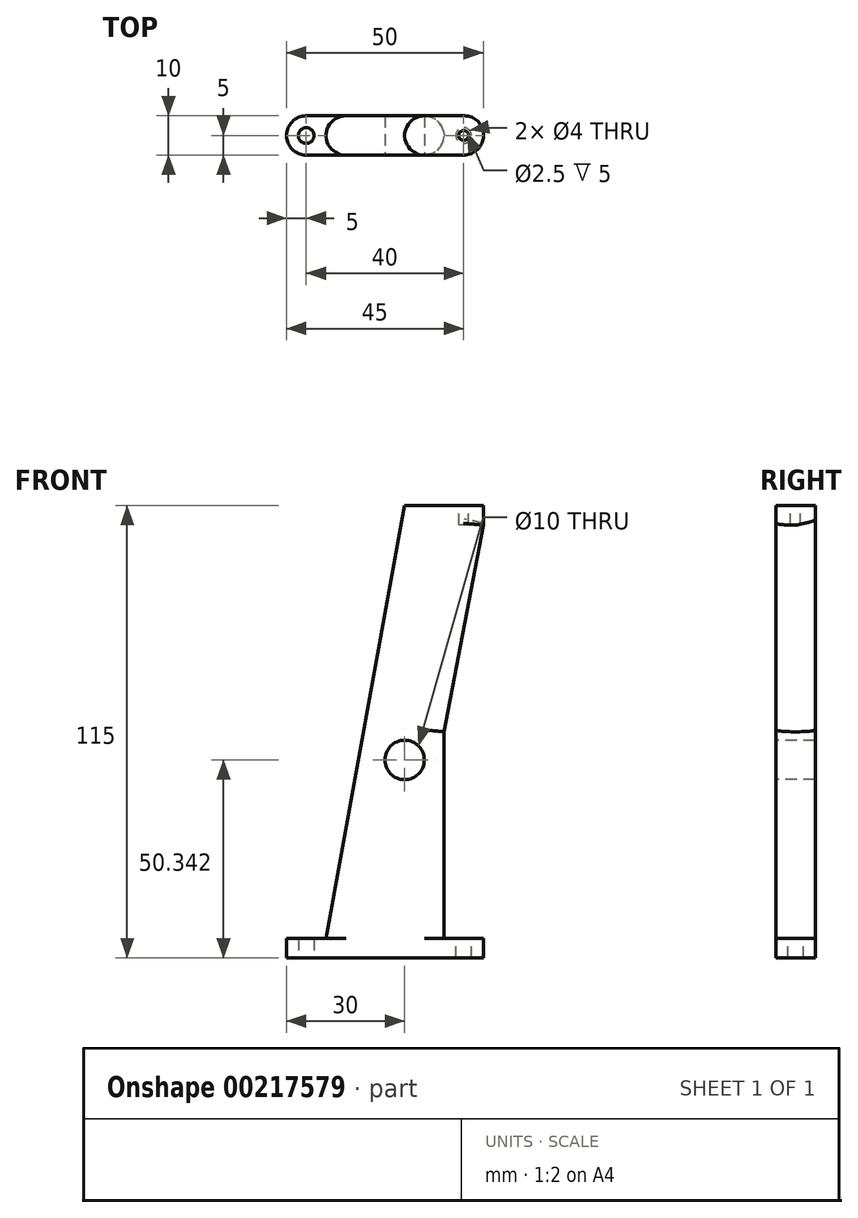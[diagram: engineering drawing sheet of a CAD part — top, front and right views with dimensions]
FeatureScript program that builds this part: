
annotation { "Feature Type Name" : "Feature", "Feature Type Description" : "" }
export const myFeature = defineFeature(function(context is Context, id is Id, definition is map)
    precondition{}
    {
        {
            var Q0;
            Q0=qCreatedBy(makeId("Front.planeOp"),FACE);
            var sketch = newSketch(context, id + "F0", { "sketchPlane" : qUnion([Q0])});
            skLineSegment(sketch, "E0.bottom", {"start": v(0, 0) * mm, "end": v(10, 0) * mm});
            skLineSegment(sketch, "E0.top", {"start": v(0, 115) * mm, "end": v(10, 115) * mm});
            skLineSegment(sketch, "E0.left", {"start": v(0, 0) * mm, "end": v(0, 115) * mm});
            skLineSegment(sketch, "E0.right", {"start": v(10, 5) * mm, "end": v(10, 110) * mm});
            skLineSegment(sketch, "E1.bottom", {"start": v(10, 115) * mm, "end": v(20, 115) * mm});
            skLineSegment(sketch, "E1.top", {"start": v(10, 110) * mm, "end": v(20, 110) * mm});
            skLineSegment(sketch, "E1.right", {"start": v(20, 115) * mm, "end": v(20, 110) * mm});
            skLineSegment(sketch, "E2.bottom", {"start": v(10, 0) * mm, "end": v(20, 0) * mm});
            skLineSegment(sketch, "E2.top", {"start": v(10, 5) * mm, "end": v(20, 5) * mm});
            skLineSegment(sketch, "E2.right", {"start": v(20, 0) * mm, "end": v(20, 5) * mm});
            skSolve(sketch);
        }
        {
            var Q0;
            Q0=makeQuery(id+"F0.imprint","IMPRINT",FACE,{"disambiguationData":[TD([[makeQuery(id+"F0.imprint","IMPRINT",EDGE,{"derivedFrom":sQuery(id+"F0.wireOp",EDGE,"E0.bottom")}),1.0]])]});
            extrude(context, id + "F1", {"entities" : qUnion([Q0]), "depth" : 10 * mm});
        }
        {
            var Q0;
            Q0=makeQuery(id+"F1.opExtrude","SWEPT_FACE",FACE,{"disambiguationData":[OSD([sQuery(id+"F0.wireOp",EDGE,"E0.top"),sQuery(id+"F0.wireOp",EDGE,"E1.bottom")])]});
            var sketch = newSketch(context, id + "F2", { "sketchPlane" : qUnion([Q0])});
            skLineSegment(sketch, "E3.bottom", {"start": v(20, -10) * mm, "end": v(15, -10) * mm, "construction": true});
            skLineSegment(sketch, "E3.top", {"start": v(20, -5) * mm, "end": v(15, -5) * mm, "construction": true});
            skLineSegment(sketch, "E3.left", {"start": v(20, -10) * mm, "end": v(20, -5) * mm, "construction": true});
            skLineSegment(sketch, "E3.right", {"start": v(15, -10) * mm, "end": v(15, -5) * mm, "construction": true});
            skCircle(sketch, "E4", {"center": v(15, -5) * mm, "radius": 2 * mm});
            skLineSegment(sketch, "E5.bottom", {"start": v(15, -10) * mm, "end": v(5, -10) * mm});
            skLineSegment(sketch, "E5.top", {"start": v(15.2, 0) * mm, "end": v(5, 0) * mm});
            skLineSegment(sketch, "E5.left", {"start": v(20, -5) * mm, "end": v(20, -4.8) * mm});
            skLineSegment(sketch, "E5.right", {"start": v(0, -5) * mm, "end": v(0, -5) * mm});
            skPoint(sketch, "E6.visualSharp", {"position": v(0, -10) * mm});
            skArc(sketch, "E6.filletArc", {"start": v(0, -5) * mm, "mid": v(1.46, -8.54) * mm, "end": v(5, -10) * mm});
            skPoint(sketch, "E7.visualSharp", {"position": v(0, 0) * mm});
            skArc(sketch, "E7.filletArc", {"start": v(5, 0) * mm, "mid": v(1.46, -1.46) * mm, "end": v(0, -5) * mm});
            skPoint(sketch, "E8.visualSharp", {"position": v(20, -10) * mm});
            skArc(sketch, "E8.filletArc", {"start": v(15, -10) * mm, "mid": v(18.54, -8.54) * mm, "end": v(20, -5) * mm});
            skPoint(sketch, "E9.visualSharp", {"position": v(20, 0) * mm});
            skArc(sketch, "E9.filletArc", {"start": v(20, -4.8) * mm, "mid": v(18.6, -1.4) * mm, "end": v(15.2, 0) * mm});
            skSolve(sketch);
        }
        {
            var Q0;
            {var subQ0=sQuery(id+"F2.wireOp",EDGE,"E6.filletArc");Q0=makeQuery(id+"F2.imprint","IMPRINT",FACE,{"disambiguationData":[TD([[makeQuery(id+"F2.imprint","IMPRINT",EDGE,{"derivedFrom":subQ0}),-1.0]])]});}
            var Q1;
            {var subQ0=sQuery(id+"F2.wireOp",EDGE,"E7.filletArc");Q1=makeQuery(id+"F2.imprint","IMPRINT",FACE,{"disambiguationData":[TD([[makeQuery(id+"F2.imprint","IMPRINT",EDGE,{"derivedFrom":subQ0}),-1.0]])]});}
            var Q2;
            {var subQ0=sQuery(id+"F2.wireOp",EDGE,"E9.filletArc");Q2=makeQuery(id+"F2.imprint","IMPRINT",FACE,{"disambiguationData":[TD([[makeQuery(id+"F2.imprint","IMPRINT",EDGE,{"derivedFrom":subQ0}),-1.0]])]});}
            var Q3;
            {var subQ0=sQuery(id+"F2.wireOp",EDGE,"E8.filletArc");Q3=makeQuery(id+"F2.imprint","IMPRINT",FACE,{"disambiguationData":[TD([[makeQuery(id+"F2.imprint","IMPRINT",EDGE,{"derivedFrom":subQ0}),-1.0]])]});}
            var Q4;
            Q4=makeQuery(id+"F2.imprint","IMPRINT",FACE,{"disambiguationData":[TD([[makeQuery(id+"F2.imprint","IMPRINT",EDGE,{"derivedFrom":sQuery(id+"F2.wireOp",EDGE,"E4")}),1.0]])]});
            extrude(context, id + "F3", {"entities" : qUnion([Q0, Q1, Q2, Q3, Q4]), "operationType" : NewBodyOperationType.REMOVE, "endBound" : BoundingType.THROUGH_ALL, "oppositeDirection" : true, "depth" : 25 * mm});
        }
        {
            var Q0;
            Q0=makeQuery(id+"F1.opExtrude","SWEPT_FACE",FACE,{"disambiguationData":[OSD([sQuery(id+"F0.wireOp",EDGE,"E0.top"),sQuery(id+"F0.wireOp",EDGE,"E1.bottom")])]});
            var sketch = newSketch(context, id + "F4", { "sketchPlane" : qUnion([Q0])});
            skCircle(sketch, "E10", {"center": v(15, -5) * mm, "radius": 3 * mm});
            skCircle(sketch, "E11", {"center": v(15, -5) * mm, "radius": 1.25 * mm});
            skSolve(sketch);
        }
        {
            var Q0;
            Q0=makeQuery(id+"F4.imprint","IMPRINT",FACE,{"disambiguationData":[TD([[makeQuery(id+"F4.imprint","IMPRINT",EDGE,{"derivedFrom":sQuery(id+"F4.wireOp",EDGE,"E11")}),-1.0]])]});
            extrude(context, id + "F5", {"entities" : qUnion([Q0]), "operationType" : NewBodyOperationType.ADD, "oppositeDirection" : true, "depth" : 5 * mm});
        }
        {
            var Q0;
            Q0=makeQuery(id+"F1.opExtrude","SWEPT_FACE",FACE,{"disambiguationData":[OSD([sQuery(id+"F0.wireOp",EDGE,"E0.bottom"),sQuery(id+"F0.wireOp",EDGE,"E2.bottom")])]});
            var sketch = newSketch(context, id + "F6", { "sketchPlane" : qUnion([Q0])});
            skLineSegment(sketch, "E12.bottom", {"start": v(5, 0) * mm, "end": v(-25, 0) * mm});
            skLineSegment(sketch, "E12.top", {"start": v(5, 10) * mm, "end": v(-25, 10) * mm});
            skLineSegment(sketch, "E12.left", {"start": v(5, 0) * mm, "end": v(5, 10) * mm});
            skLineSegment(sketch, "E12.right", {"start": v(-30, 5) * mm, "end": v(-30, 5) * mm});
            skPoint(sketch, "E13.visualSharp", {"position": v(-30, 0) * mm});
            skArc(sketch, "E13.filletArc", {"start": v(-30, 5) * mm, "mid": v(-28.54, 1.46) * mm, "end": v(-25, 0) * mm});
            skPoint(sketch, "E14.visualSharp", {"position": v(-30, 10) * mm});
            skArc(sketch, "E14.filletArc", {"start": v(-25, 10) * mm, "mid": v(-28.54, 8.54) * mm, "end": v(-30, 5) * mm});
            skCircle(sketch, "E15", {"center": v(-25, 5) * mm, "radius": 2 * mm});
            skSolve(sketch);
        }
        {
            var Q0;
            Q0=makeQuery(id+"F6.imprint","IMPRINT",FACE,{"disambiguationData":[TD([[makeQuery(id+"F6.imprint","IMPRINT",EDGE,{"derivedFrom":sQuery(id+"F6.wireOp",EDGE,"E12.bottom")}),-1.0]])]});
            extrude(context, id + "F7", {"entities" : qUnion([Q0]), "operationType" : NewBodyOperationType.ADD, "oppositeDirection" : true, "depth" : 5 * mm});
        }
        {
            var Q0;
            Q0=makeQuery(id+"F7.boolean.opBoolean","MERGE",FACE,{"derivedFrom":[makeQuery(id+"F1.opExtrude","CAP_FACE",FACE,{"disambiguationData":[OSD([sQuery(id+"F0.wireOp",EDGE,"E0.bottom"),sQuery(id+"F0.wireOp",EDGE,"E0.top"),sQuery(id+"F0.wireOp",EDGE,"E0.left"),sQuery(id+"F0.wireOp",EDGE,"E0.right"),sQuery(id+"F0.wireOp",EDGE,"E1.bottom"),sQuery(id+"F0.wireOp",EDGE,"E1.top"),sQuery(id+"F0.wireOp",EDGE,"E1.right"),sQuery(id+"F0.wireOp",EDGE,"E2.bottom"),sQuery(id+"F0.wireOp",EDGE,"E2.top"),sQuery(id+"F0.wireOp",EDGE,"E2.right")])],"isStart":false}),makeQuery(id+"F7.opExtrude","SWEPT_FACE",FACE,{"disambiguationData":[OSD([sQuery(id+"F6.wireOp",EDGE,"E12.top")])]})]});
            var sketch = newSketch(context, id + "F8", { "sketchPlane" : qUnion([Q0])});
            skLineSegment(sketch, "E16", {"start": v(-25, 5) * mm, "end": v(-20, 5) * mm, "construction": true});
            skLineSegment(sketch, "E17", {"start": v(-20, 5) * mm, "end": v(0, 115) * mm});
            skLineSegment(sketch, "E18", {"start": v(0, 115) * mm, "end": v(5, 115) * mm});
            skLineSegment(sketch, "E19", {"start": v(5, 115) * mm, "end": v(5, 5) * mm});
            skLineSegment(sketch, "E20", {"start": v(5, 5) * mm, "end": v(-20, 5) * mm});
            skSolve(sketch);
        }
        {
            var Q0;
            Q0=makeQuery(id+"F8.imprint","IMPRINT",FACE,{"disambiguationData":[TD([[makeQuery(id+"F8.imprint","IMPRINT",EDGE,{"derivedFrom":sQuery(id+"F8.wireOp",EDGE,"E17")}),-1.0]])]});
            extrude(context, id + "F9", {"entities" : qUnion([Q0]), "operationType" : NewBodyOperationType.ADD, "oppositeDirection" : true, "depth" : 10 * mm});
        }
        {
            var Q0;
            Q0=makeQuery(id+"F9.opExtrude","CAP_EDGE",EDGE,{"disambiguationData":[OSD([sQuery(id+"F8.wireOp",EDGE,"E17")])],"isStart":false});
            var Q1;
            Q1=makeQuery(id+"F9.opExtrude","CAP_EDGE",EDGE,{"disambiguationData":[OSD([sQuery(id+"F8.wireOp",EDGE,"E17")])],"isStart":true});
            fillet(context, id + "F10", {"entities" : qUnion([Q0, Q1]), "radius" : 5 * mm, "tangentPropagation" : true, "allowEdgeOverflow" : false});
        }
        {
            var Q0;
            Q0=makeQuery(id+"F9.boolean.opBoolean","MERGE",FACE,{"derivedFrom":[makeQuery(id+"F7.boolean.opBoolean","MERGE",FACE,{"derivedFrom":[makeQuery(id+"F1.opExtrude","CAP_FACE",FACE,{"disambiguationData":[OSD([sQuery(id+"F0.wireOp",EDGE,"E0.bottom"),sQuery(id+"F0.wireOp",EDGE,"E0.top"),sQuery(id+"F0.wireOp",EDGE,"E0.left"),sQuery(id+"F0.wireOp",EDGE,"E0.right"),sQuery(id+"F0.wireOp",EDGE,"E1.bottom"),sQuery(id+"F0.wireOp",EDGE,"E1.top"),sQuery(id+"F0.wireOp",EDGE,"E1.right"),sQuery(id+"F0.wireOp",EDGE,"E2.bottom"),sQuery(id+"F0.wireOp",EDGE,"E2.top"),sQuery(id+"F0.wireOp",EDGE,"E2.right")])],"isStart":false}),makeQuery(id+"F7.opExtrude","SWEPT_FACE",FACE,{"disambiguationData":[OSD([sQuery(id+"F6.wireOp",EDGE,"E12.top")])]})]}),makeQuery(id+"F9.opExtrude","CAP_FACE",FACE,{"disambiguationData":[OSD([sQuery(id+"F8.wireOp",EDGE,"E17"),sQuery(id+"F8.wireOp",EDGE,"E18"),sQuery(id+"F8.wireOp",EDGE,"E19"),sQuery(id+"F8.wireOp",EDGE,"E20")])],"isStart":true})]});
            var sketch = newSketch(context, id + "F11", { "sketchPlane" : qUnion([Q0])});
            skCircle(sketch, "E21", {"center": v(0, 50.34) * mm, "radius": 5 * mm});
            skSolve(sketch);
        }
        {
            var Q0;
            Q0=makeQuery(id+"F11.imprint","IMPRINT",FACE,{"disambiguationData":[TD([[makeQuery(id+"F11.imprint","IMPRINT",EDGE,{"derivedFrom":sQuery(id+"F11.wireOp",EDGE,"E21")}),1.0]])]});
            extrude(context, id + "F12", {"entities" : qUnion([Q0]), "operationType" : NewBodyOperationType.REMOVE, "endBound" : BoundingType.THROUGH_ALL, "oppositeDirection" : true, "depth" : 25 * mm});
        }
        {
            var Q0;
            Q0=makeQuery(id+"F9.boolean.opBoolean","MERGE",FACE,{"derivedFrom":[makeQuery(id+"F7.boolean.opBoolean","MERGE",FACE,{"derivedFrom":[makeQuery(id+"F1.opExtrude","CAP_FACE",FACE,{"disambiguationData":[OSD([sQuery(id+"F0.wireOp",EDGE,"E0.bottom"),sQuery(id+"F0.wireOp",EDGE,"E0.top"),sQuery(id+"F0.wireOp",EDGE,"E0.left"),sQuery(id+"F0.wireOp",EDGE,"E0.right"),sQuery(id+"F0.wireOp",EDGE,"E1.bottom"),sQuery(id+"F0.wireOp",EDGE,"E1.top"),sQuery(id+"F0.wireOp",EDGE,"E1.right"),sQuery(id+"F0.wireOp",EDGE,"E2.bottom"),sQuery(id+"F0.wireOp",EDGE,"E2.top"),sQuery(id+"F0.wireOp",EDGE,"E2.right")])],"isStart":true}),makeQuery(id+"F7.opExtrude","SWEPT_FACE",FACE,{"disambiguationData":[OSD([sQuery(id+"F6.wireOp",EDGE,"E12.bottom")])]})]}),makeQuery(id+"F9.opExtrude","CAP_FACE",FACE,{"disambiguationData":[OSD([sQuery(id+"F8.wireOp",EDGE,"E17"),sQuery(id+"F8.wireOp",EDGE,"E18"),sQuery(id+"F8.wireOp",EDGE,"E19"),sQuery(id+"F8.wireOp",EDGE,"E20")])],"isStart":false})]});
            var sketch = newSketch(context, id + "F13", { "sketchPlane" : qUnion([Q0])});
            skLineSegment(sketch, "E22", {"start": v(-10, 57.5) * mm, "end": v(-10, 110) * mm});
            skLineSegment(sketch, "E23", {"start": v(-10, 110) * mm, "end": v(-20, 110) * mm});
            skLineSegment(sketch, "E24", {"start": v(-20, 110) * mm, "end": v(-10, 57.5) * mm});
            skSolve(sketch);
        }
        {
            var Q0;
            {var subQ0=sQuery(id+"F13.wireOp",EDGE,"E22");Q0=makeQuery(id+"F13.imprint","IMPRINT",FACE,{"disambiguationData":[TD([[makeQuery(id+"F13.imprint","IMPRINT",EDGE,{"derivedFrom":subQ0}),1.0]])]});}
            extrude(context, id + "F14", {"entities" : qUnion([Q0]), "operationType" : NewBodyOperationType.ADD, "oppositeDirection" : true, "depth" : 10 * mm});
        }
        {
            var Q0;
            Q0=makeQuery(id+"F14.opExtrude","CAP_EDGE",EDGE,{"disambiguationData":[OSD([sQuery(id+"F13.wireOp",EDGE,"E24")])],"isStart":true});
            var Q1;
            Q1=makeQuery(id+"F14.opExtrude","CAP_EDGE",EDGE,{"disambiguationData":[OSD([sQuery(id+"F13.wireOp",EDGE,"E24")])],"isStart":false});
            fillet(context, id + "F15", {"entities" : qUnion([Q0, Q1]), "radius" : 5 * mm, "tangentPropagation" : true, "allowEdgeOverflow" : false});
        }
        {
            var Q0;
            Q0=makeQuery(id+"F1.opExtrude","CAP_EDGE",EDGE,{"disambiguationData":[OSD([sQuery(id+"F0.wireOp",EDGE,"E0.right")])],"isStart":true});
            var Q1;
            Q1=makeQuery(id+"F1.opExtrude","CAP_EDGE",EDGE,{"disambiguationData":[OSD([sQuery(id+"F0.wireOp",EDGE,"E0.right")])],"isStart":false});
            fillet(context, id + "F16", {"entities" : qUnion([Q0, Q1]), "radius" : 5 * mm, "tangentPropagation" : true, "allowEdgeOverflow" : false});
        }
    });
